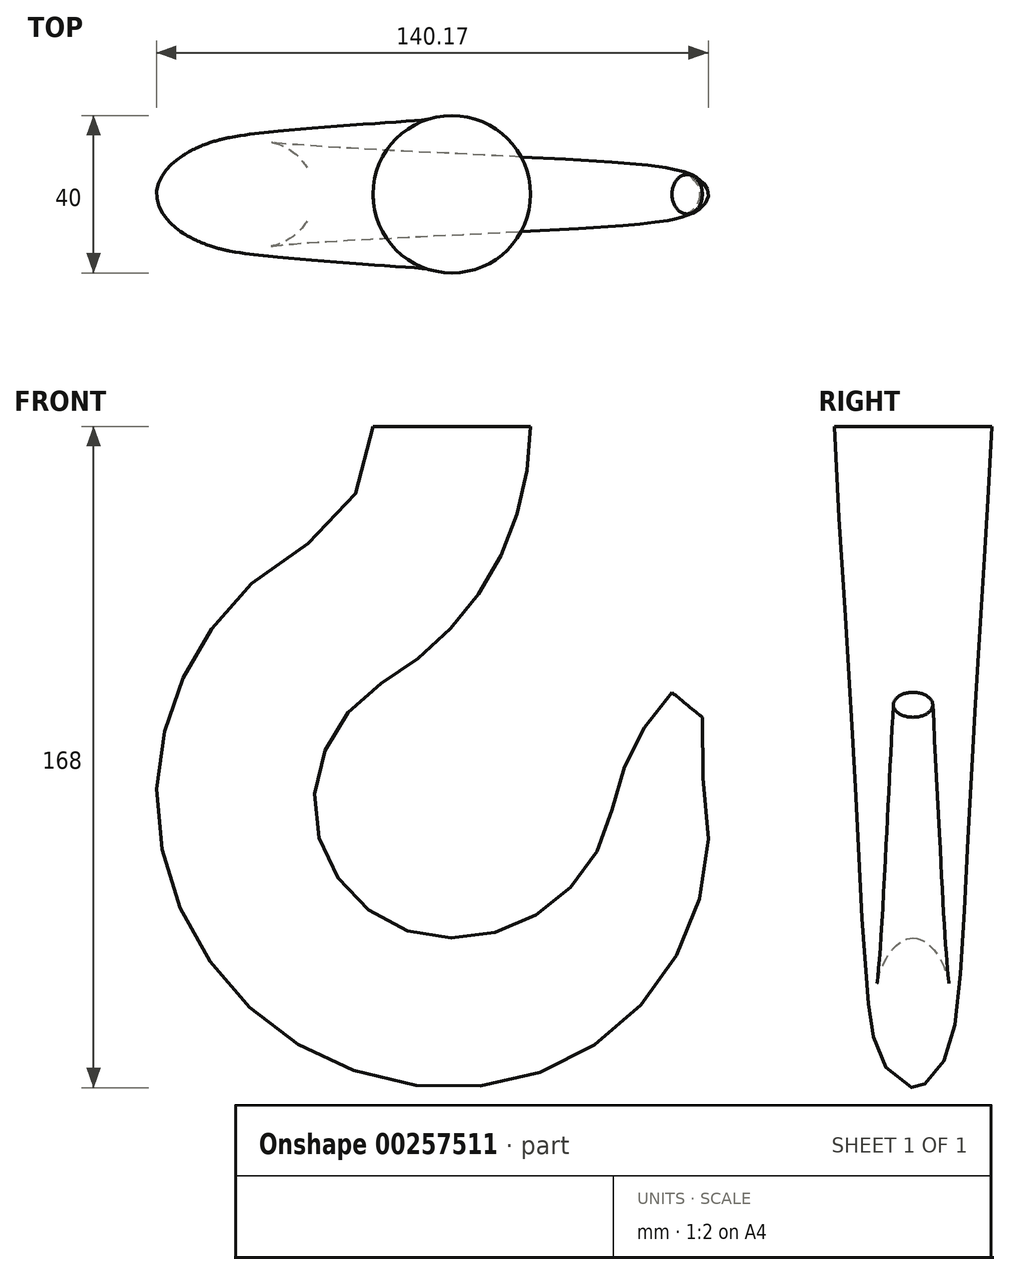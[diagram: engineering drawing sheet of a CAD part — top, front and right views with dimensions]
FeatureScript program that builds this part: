
annotation { "Feature Type Name" : "Feature", "Feature Type Description" : "" }
export const myFeature = defineFeature(function(context is Context, id is Id, definition is map)
    precondition{}
    {
        {
            var Q0;
            Q0=qCreatedBy(makeId("Front.planeOp"),FACE);
            var sketch = newSketch(context, id + "F0", { "sketchPlane" : qUnion([Q0])});
            skLineSegment(sketch, "E0", {"start": v(0, 0) * mm, "end": v(0, 95) * mm, "construction": true});
            skLineSegment(sketch, "E1", {"start": v(-20, 95) * mm, "end": v(-55, 95) * mm, "construction": true});
            skArc(sketch, "E2", {"start": v(-20, 95) * mm, "mid": v(-25.35, 76.4) * mm, "end": v(-39.77, 63.49) * mm});
            skLineSegment(sketch, "E3", {"start": v(-75, 10.04) * mm, "end": v(-75, -15.52) * mm, "construction": true});
            skArc(sketch, "E4", {"start": v(-75, 0) * mm, "mid": v(-65.99, 35.64) * mm, "end": v(-41.12, 62.72) * mm});
            skArc(sketch, "E5", {"start": v(-39.77, 63.49) * mm, "mid": v(-40.46, 63.13) * mm, "end": v(-41.12, 62.72) * mm});
            skLineSegment(sketch, "E6", {"start": v(-15, -35) * mm, "end": v(12.04, -35) * mm, "construction": true});
            skArc(sketch, "E7", {"start": v(0, -35) * mm, "mid": v(-24.75, -24.75) * mm, "end": v(-35, 0) * mm});
            skLineSegment(sketch, "E8", {"start": v(0.17, -73) * mm, "end": v(32.58, -73) * mm, "construction": true});
            skArc(sketch, "E9", {"start": v(0.17, -73) * mm, "mid": v(-52.22, -51.75) * mm, "end": v(-75, 0) * mm});
            skArc(sketch, "E10", {"start": v(0.17, -73) * mm, "mid": v(50.29, -49.4) * mm, "end": v(64, 4.29) * mm});
            skArc(sketch, "E11", {"start": v(64, 4.29) * mm, "mid": v(63.1, 12.69) * mm, "end": v(63.65, 21.12) * mm});
            skArc(sketch, "E12", {"start": v(20, 95) * mm, "mid": v(10.15, 57.84) * mm, "end": v(-16.81, 30.45) * mm});
            skArc(sketch, "E13", {"start": v(-16.81, 30.45) * mm, "mid": v(-29.78, 17.54) * mm, "end": v(-35, 0) * mm});
            skArc(sketch, "E14", {"start": v(55.9, 27.44) * mm, "mid": v(46.4, 13.97) * mm, "end": v(40.92, -1.57) * mm});
            skArc(sketch, "E15", {"start": v(0, -35) * mm, "mid": v(26.42, -25.58) * mm, "end": v(40.92, -1.57) * mm});
            skLineSegment(sketch, "E16", {"start": v(63.65, 21.12) * mm, "end": v(55.9, 27.44) * mm});
            skCircle(sketch, "E17", {"center": v(59.77, 24.28) * mm, "radius": 5 * mm, "construction": true});
            skLineSegment(sketch, "E18", {"start": v(-20, 95) * mm, "end": v(20, 95) * mm});
            skSolve(sketch);
        }
        {
            var Q0;
            Q0=sQuery(id+"F0.wireOp",EDGE,"E16");
            cPlane(context, id + "F1", {"entities" : qUnion([Q0]), "cplaneType" : CPlaneType.LINE_ANGLE, "offset" : 25 * mm, "angle" : 90 * degree, "width" : 150 * mm, "height" : 150 * mm});
        }
        {
            var Q0;
            Q0=sQuery(id+"F0.wireOp",EDGE,"E18");
            cPlane(context, id + "F2", {"entities" : qUnion([Q0]), "cplaneType" : CPlaneType.LINE_ANGLE, "offset" : 25 * mm, "angle" : 90 * degree, "width" : 150 * mm, "height" : 150 * mm});
        }
        {
            var Q0;
            Q0=qCreatedBy(id+"F2.planeOp",FACE);
            var sketch = newSketch(context, id + "F3", { "sketchPlane" : qUnion([Q0])});
            skLineSegment(sketch, "E19.0", {"start": v(-20, 0) * mm, "end": v(20, 0) * mm, "construction": true});
            skCircle(sketch, "E20", {"center": v(0, 0) * mm, "radius": 20 * mm});
            skSolve(sketch);
        }
        {
            var Q0;
            Q0=qCreatedBy(id+"F1.planeOp",FACE);
            var sketch = newSketch(context, id + "F4", { "sketchPlane" : qUnion([Q0])});
            skLineSegment(sketch, "E21.0", {"start": v(35.96, 0) * mm, "end": v(25.96, 0) * mm, "construction": true});
            skCircle(sketch, "E22", {"center": v(30.96, 0) * mm, "radius": 5 * mm});
            skSolve(sketch);
        }
        {
            var Q0;
            Q0=qCreatedBy(makeId("Front.planeOp"),FACE);
            cPlane(context, id + "F5", {"entities" : qUnion([Q0]), "cplaneType" : CPlaneType.OFFSET, "offset" : 0 * mm, "width" : 150 * mm, "height" : 150 * mm});
        }
        {
            var Q0;
            Q0=qCreatedBy(id+"F5.planeOp",FACE);
            var sketch = newSketch(context, id + "F6", { "sketchPlane" : qUnion([Q0])});
            skArc(sketch, "E23.0", {"start": v(-20, 95) * mm, "mid": v(-25.35, 76.4) * mm, "end": v(-39.77, 63.49) * mm});
            skArc(sketch, "E24.0", {"start": v(-39.77, 63.49) * mm, "mid": v(-40.46, 63.13) * mm, "end": v(-41.12, 62.72) * mm});
            skArc(sketch, "E25.0", {"start": v(-75, 0) * mm, "mid": v(-65.99, 35.64) * mm, "end": v(-41.12, 62.72) * mm});
            skArc(sketch, "E26.0", {"start": v(0.17, -73) * mm, "mid": v(-52.22, -51.75) * mm, "end": v(-75, 0) * mm});
            skArc(sketch, "E27.0", {"start": v(0.17, -73) * mm, "mid": v(50.29, -49.4) * mm, "end": v(64, 4.29) * mm});
            skArc(sketch, "E28.0", {"start": v(64, 4.29) * mm, "mid": v(63.1, 12.69) * mm, "end": v(63.65, 21.12) * mm});
            skSolve(sketch);
        }
        {
            var Q0;
            Q0=qCreatedBy(id+"F5.planeOp",FACE);
            var sketch = newSketch(context, id + "F7", { "sketchPlane" : qUnion([Q0])});
            skArc(sketch, "E29.0", {"start": v(20, 95) * mm, "mid": v(10.15, 57.84) * mm, "end": v(-16.81, 30.45) * mm});
            skArc(sketch, "E30.0", {"start": v(-16.81, 30.45) * mm, "mid": v(-29.78, 17.54) * mm, "end": v(-35, 0) * mm});
            skArc(sketch, "E31.0", {"start": v(0, -35) * mm, "mid": v(-24.75, -24.75) * mm, "end": v(-35, 0) * mm});
            skPoint(sketch, "E32.0", {"position": v(26.42, -25.58) * mm});
            skArc(sketch, "E33.0", {"start": v(0, -35) * mm, "mid": v(26.42, -25.58) * mm, "end": v(40.92, -1.57) * mm});
            skArc(sketch, "E34.0", {"start": v(55.9, 27.44) * mm, "mid": v(46.4, 13.97) * mm, "end": v(40.92, -1.57) * mm});
            skSolve(sketch);
        }
        {
            var Q0;
            Q0=makeQuery(id+"F3.imprint","IMPRINT",FACE,{"disambiguationData":[TD([[makeQuery(id+"F3.imprint","IMPRINT",EDGE,{"derivedFrom":sQuery(id+"F3.wireOp",EDGE,"E20")}),1.0]])]});
            var Q1;
            Q1=makeQuery(id+"F4.imprint","IMPRINT",FACE,{"disambiguationData":[TD([[makeQuery(id+"F4.imprint","IMPRINT",EDGE,{"derivedFrom":sQuery(id+"F4.wireOp",EDGE,"E22")}),1.0]])]});
            var Q2;
            Q2 = qConstructionFilter(qBodyType(qCreatedBy(id + "F7" ,EDGE), BodyType.WIRE), ConstructionObject.NO);
            var Q3;
            Q3 = qConstructionFilter(qBodyType(qCreatedBy(id + "F6" ,EDGE), BodyType.WIRE), ConstructionObject.NO);
            loft(context, id + "F8", {"addGuides" : true, "sheetProfilesArray" : [{ "sheetProfileEntities" : qUnion([Q0]) }, { "sheetProfileEntities" : qUnion([Q1]) }], "guidesArray" : [{ "guideEntities" : qUnion([Q2]), "guideDerivativeType" : LoftGuideDerivativeType.DEFAULT, "guideDerivativeMagnitude" : 1 }, { "guideEntities" : qUnion([Q3]), "guideDerivativeType" : LoftGuideDerivativeType.DEFAULT, "guideDerivativeMagnitude" : 1 }]});
        }
    });
